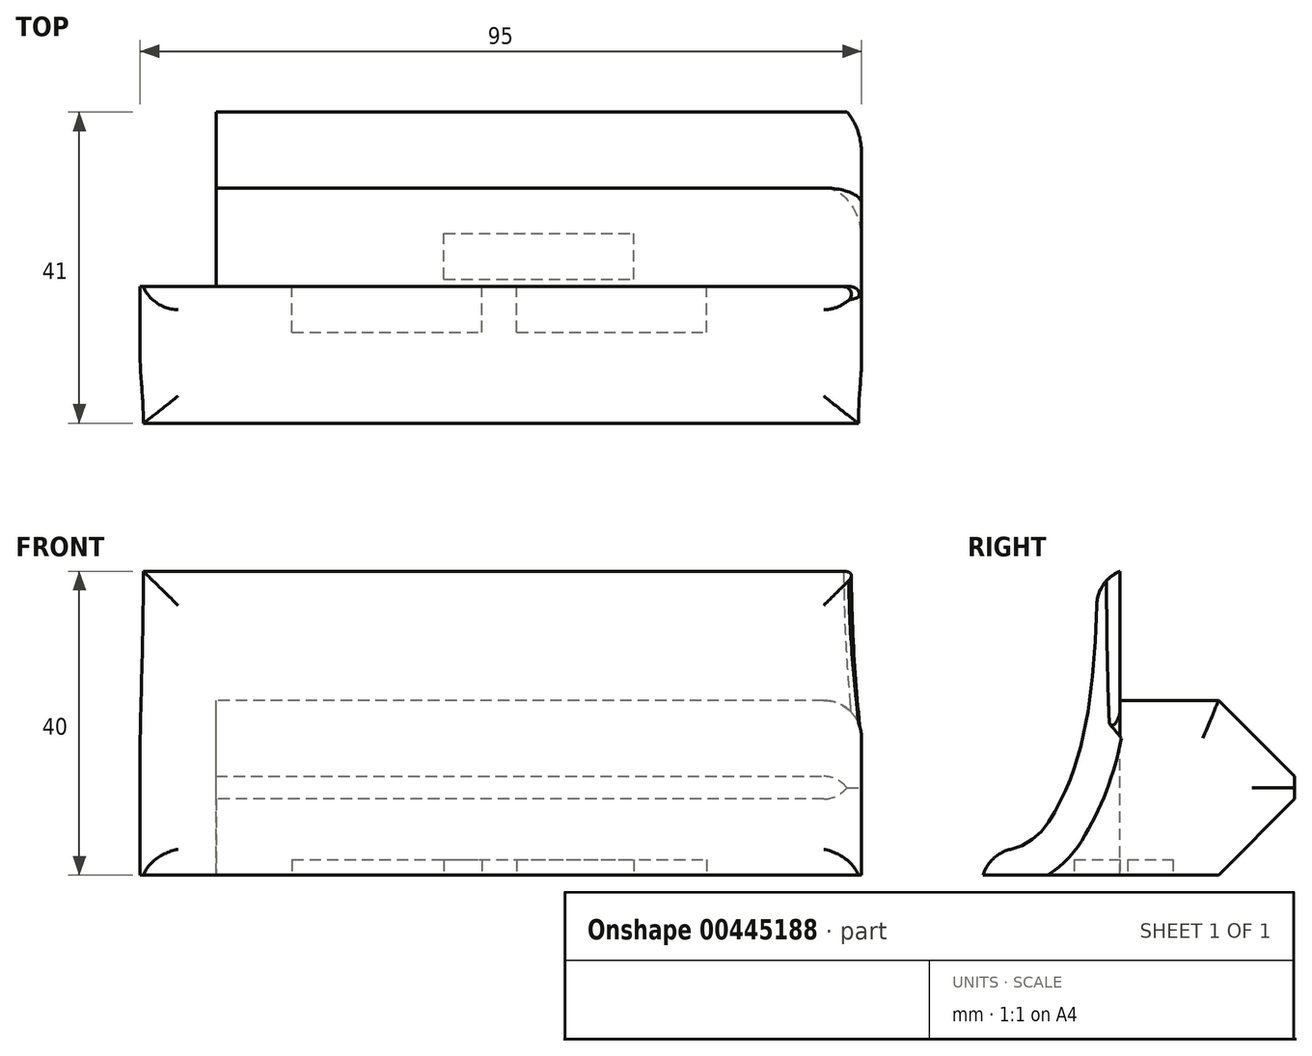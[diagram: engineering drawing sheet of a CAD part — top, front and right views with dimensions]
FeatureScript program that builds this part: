
annotation { "Feature Type Name" : "Feature", "Feature Type Description" : "" }
export const myFeature = defineFeature(function(context is Context, id is Id, definition is map)
    precondition{}
    {
        {
            var Q0;
            Q0=qCreatedBy(makeId("Right.planeOp"),FACE);
            var sketch = newSketch(context, id + "F0", { "sketchPlane" : qUnion([Q0])});
            skLineSegment(sketch, "E0", {"start": v(0, 0) * mm, "end": v(-18, 0) * mm});
            skLineSegment(sketch, "E1", {"start": v(0, 0) * mm, "end": v(0, 40) * mm});
            skLineSegment(sketch, "E2", {"start": v(0, 0) * mm, "end": v(-8.49, 8.49) * mm, "construction": true});
            skLineSegment(sketch, "E3", {"start": v(-18, 0) * mm, "end": v(-18, 3) * mm});
            skLineSegment(sketch, "E4", {"start": v(0, 40) * mm, "end": v(-3, 40) * mm});
            skFitSpline(sketch, "E5", {"points": [v(-18, 3) * mm, v(-8.49, 8.49) * mm, v(-3, 40) * mm], "startDerivative": vector(48.72, 0) * mm, "endDerivative": vector(0, 90.4) * mm});
            skLineSegment(sketch, "E6", {"start": v(0, 0) * mm, "end": v(23, 0) * mm});
            skLineSegment(sketch, "E7", {"start": v(23, 0) * mm, "end": v(23, 23) * mm});
            skLineSegment(sketch, "E8", {"start": v(23, 23) * mm, "end": v(0, 23) * mm});
            skSolve(sketch);
        }
        {
            var Q0;
            Q0 = qSketchRegion(id + "F0", true);
            extrude(context, id + "F1", {"entities" : qUnion([Q0]), "depth" : 85 * mm});
        }
        {
            var Q0;
            {var subQ3=sQuery(id+"F0.wireOp",EDGE,"E0");Q0=makeQuery(id+"F0.imprint","IMPRINT",FACE,{"disambiguationData":[TD([[makeQuery(id+"F0.imprint","IMPRINT",EDGE,{"derivedFrom":subQ3}),-1.0]])]});}
            extrude(context, id + "F2", {"entities" : qUnion([Q0]), "operationType" : NewBodyOperationType.ADD, "oppositeDirection" : true, "depth" : 10 * mm});
        }
        {
            var Q0;
            Q0=makeQuery(id+"F1.opExtrude","SWEPT_EDGE",EDGE,{"disambiguationData":[OSD([sQuery(id+"F0.wireOp",EDGE,"E7"),sQuery(id+"F0.wireOp",EDGE,"E8")])]});
            var Q1;
            Q1=makeQuery(id+"F1.opExtrude","SWEPT_EDGE",EDGE,{"disambiguationData":[OSD([sQuery(id+"F0.wireOp",EDGE,"E6"),sQuery(id+"F0.wireOp",EDGE,"E7")])]});
            chamfer(context, id + "F3", {"entities" : qUnion([Q0, Q1]), "width" : 10 * mm, "tangentPropagation" : true});
        }
        {
            var Q0;
            {var subQ0=sQuery(id+"F0.wireOp",EDGE,"E5");var subQ1=sQuery(id+"F0.wireOp",EDGE,"E3");Q0=makeQuery(id+"F2.boolean.opBoolean","MERGE",EDGE,{"derivedFrom":[makeQuery(id+"F1.opExtrude","SWEPT_EDGE",EDGE,{"disambiguationData":[OSD([subQ1,subQ0])]}),makeQuery(id+"F2.opExtrude","SWEPT_EDGE",EDGE,{"disambiguationData":[OSD([subQ1,subQ0])]})]});}
            var Q1;
            {var subQ0=sQuery(id+"F0.wireOp",EDGE,"E5");var subQ1=sQuery(id+"F0.wireOp",EDGE,"E4");Q1=makeQuery(id+"F2.boolean.opBoolean","MERGE",EDGE,{"derivedFrom":[makeQuery(id+"F1.opExtrude","SWEPT_EDGE",EDGE,{"disambiguationData":[OSD([subQ1,subQ0])]}),makeQuery(id+"F2.opExtrude","SWEPT_EDGE",EDGE,{"disambiguationData":[OSD([subQ1,subQ0])]})]});}
            var Q2;
            Q2=makeQuery(id+"F2.opExtrude","CAP_EDGE",EDGE,{"disambiguationData":[OSD([sQuery(id+"F0.wireOp",EDGE,"E5")])],"isStart":false});
            var Q3;
            Q3=makeQuery(id+"F1.opExtrude","CAP_EDGE",EDGE,{"disambiguationData":[OSD([sQuery(id+"F0.wireOp",EDGE,"E5")])],"isStart":false});
            var Q4;
            Q4=makeQuery(id+"F1.opExtrude","CAP_EDGE",EDGE,{"disambiguationData":[OSD([sQuery(id+"F0.wireOp",EDGE,"E8")])],"isStart":false});
            var Q5;
            Q5=makeQuery(id+"F1.opExtrude","CAP_EDGE",EDGE,{"disambiguationData":[OSD([sQuery(id+"F0.wireOp",EDGE,"E7")])],"isStart":false});
            var Q6;
            {var subQ0=sQuery(id+"F0.wireOp",EDGE,"E8");var subQ1=sQuery(id+"F0.wireOp",EDGE,"E7");Q6=makeQuery(id+"F3.opChamfer","BLEND_EDGE",EDGE,{"blendedFrom":[makeQuery(id+"F1.opExtrude","SWEPT_EDGE",EDGE,{"disambiguationData":[OSD([subQ1,subQ0])]}),makeQuery(id+"F1.opExtrude","CAP_FACE",FACE,{"disambiguationData":[OSD([sQuery(id+"F0.wireOp",EDGE,"E0"),sQuery(id+"F0.wireOp",EDGE,"E1"),sQuery(id+"F0.wireOp",EDGE,"E3"),sQuery(id+"F0.wireOp",EDGE,"E4"),sQuery(id+"F0.wireOp",EDGE,"E5"),sQuery(id+"F0.wireOp",EDGE,"E6"),subQ1,subQ0])],"isStart":false})],"blendedInto":[makeQuery(id+"F1.opExtrude","CAP_FACE",FACE,{"disambiguationData":[OSD([sQuery(id+"F0.wireOp",EDGE,"E0"),sQuery(id+"F0.wireOp",EDGE,"E1"),sQuery(id+"F0.wireOp",EDGE,"E3"),sQuery(id+"F0.wireOp",EDGE,"E4"),sQuery(id+"F0.wireOp",EDGE,"E5"),sQuery(id+"F0.wireOp",EDGE,"E6"),subQ1,subQ0])],"isStart":false})]});}
            var Q7;
            {var subQ0=sQuery(id+"F0.wireOp",EDGE,"E7");var subQ1=sQuery(id+"F0.wireOp",EDGE,"E6");Q7=makeQuery(id+"F3.opChamfer","BLEND_EDGE",EDGE,{"blendedFrom":[makeQuery(id+"F1.opExtrude","SWEPT_EDGE",EDGE,{"disambiguationData":[OSD([subQ1,subQ0])]}),makeQuery(id+"F1.opExtrude","CAP_FACE",FACE,{"disambiguationData":[OSD([sQuery(id+"F0.wireOp",EDGE,"E0"),sQuery(id+"F0.wireOp",EDGE,"E1"),sQuery(id+"F0.wireOp",EDGE,"E3"),sQuery(id+"F0.wireOp",EDGE,"E4"),sQuery(id+"F0.wireOp",EDGE,"E5"),subQ1,subQ0,sQuery(id+"F0.wireOp",EDGE,"E8")])],"isStart":false})],"blendedInto":[makeQuery(id+"F1.opExtrude","CAP_FACE",FACE,{"disambiguationData":[OSD([sQuery(id+"F0.wireOp",EDGE,"E0"),sQuery(id+"F0.wireOp",EDGE,"E1"),sQuery(id+"F0.wireOp",EDGE,"E3"),sQuery(id+"F0.wireOp",EDGE,"E4"),sQuery(id+"F0.wireOp",EDGE,"E5"),subQ1,subQ0,sQuery(id+"F0.wireOp",EDGE,"E8")])],"isStart":false})]});}
            fillet(context, id + "F4", {"entities" : qUnion([Q0, Q1, Q2, Q3, Q4, Q5, Q6, Q7]), "radius" : 5 * mm, "tangentPropagation" : true, "allowEdgeOverflow" : false});
        }
        {
            var Q0;
            {var subQ0=sQuery(id+"F0.wireOp",EDGE,"E1");Q0=makeQuery(id+"F4.opFillet","BLEND_EDGE",EDGE,{"blendedFrom":[makeQuery(id+"F1.opExtrude","CAP_EDGE",EDGE,{"disambiguationData":[OSD([sQuery(id+"F0.wireOp",EDGE,"E5")])],"isStart":false}),makeQuery(id+"F2.boolean.opBoolean","MERGE",FACE,{"derivedFrom":[makeQuery(id+"F1.opExtrude","SWEPT_FACE",FACE,{"disambiguationData":[OSD([subQ0])]}),makeQuery(id+"F2.opExtrude","SWEPT_FACE",FACE,{"disambiguationData":[OSD([subQ0])]})]})],"blendedInto":[makeQuery(id+"F2.boolean.opBoolean","MERGE",FACE,{"derivedFrom":[makeQuery(id+"F1.opExtrude","SWEPT_FACE",FACE,{"disambiguationData":[OSD([subQ0])]}),makeQuery(id+"F2.opExtrude","SWEPT_FACE",FACE,{"disambiguationData":[OSD([subQ0])]})]})]});}
            var Q1;
            {var subQ0=sQuery(id+"F0.wireOp",EDGE,"E8");var subQ1=sQuery(id+"F0.wireOp",EDGE,"E7");Q1=makeQuery(id+"F3.opChamfer","BLEND_EDGE",EDGE,{"blendedFrom":[makeQuery(id+"F1.opExtrude","SWEPT_EDGE",EDGE,{"disambiguationData":[OSD([subQ1,subQ0])]}),makeQuery(id+"F1.opExtrude","CAP_FACE",FACE,{"disambiguationData":[OSD([sQuery(id+"F0.wireOp",EDGE,"E0"),sQuery(id+"F0.wireOp",EDGE,"E1"),sQuery(id+"F0.wireOp",EDGE,"E3"),sQuery(id+"F0.wireOp",EDGE,"E4"),sQuery(id+"F0.wireOp",EDGE,"E5"),sQuery(id+"F0.wireOp",EDGE,"E6"),subQ1,subQ0])],"isStart":false})],"blendedInto":[makeQuery(id+"F1.opExtrude","CAP_FACE",FACE,{"disambiguationData":[OSD([sQuery(id+"F0.wireOp",EDGE,"E0"),sQuery(id+"F0.wireOp",EDGE,"E1"),sQuery(id+"F0.wireOp",EDGE,"E3"),sQuery(id+"F0.wireOp",EDGE,"E4"),sQuery(id+"F0.wireOp",EDGE,"E5"),sQuery(id+"F0.wireOp",EDGE,"E6"),subQ1,subQ0])],"isStart":false})]});}
            fillet(context, id + "F5", {"entities" : qUnion([Q0, Q1]), "radius" : 1 * mm, "tangentPropagation" : true, "allowEdgeOverflow" : false});
        }
        {
            var Q0;
            {var subQ0=sQuery(id+"F0.wireOp",EDGE,"E0");Q0=makeQuery(id+"F2.boolean.opBoolean","MERGE",FACE,{"derivedFrom":[makeQuery(id+"F1.opExtrude","SWEPT_FACE",FACE,{"disambiguationData":[OSD([subQ0,sQuery(id+"F0.wireOp",EDGE,"E6")])]}),makeQuery(id+"F2.opExtrude","SWEPT_FACE",FACE,{"disambiguationData":[OSD([subQ0])]})]});}
            var sketch = newSketch(context, id + "F6", { "sketchPlane" : qUnion([Q0])});
            skLineSegment(sketch, "E9.bottom", {"start": v(39.6, 6) * mm, "end": v(64.6, 6) * mm});
            skLineSegment(sketch, "E9.top", {"start": v(39.6, 0) * mm, "end": v(64.6, 0) * mm});
            skLineSegment(sketch, "E9.left", {"start": v(39.6, 6) * mm, "end": v(39.6, 0) * mm});
            skLineSegment(sketch, "E9.right", {"start": v(64.6, 6) * mm, "end": v(64.6, 0) * mm});
            skLineSegment(sketch, "E10.bottom", {"start": v(30, -1) * mm, "end": v(55, -1) * mm});
            skLineSegment(sketch, "E10.top", {"start": v(30, -7) * mm, "end": v(55, -7) * mm});
            skLineSegment(sketch, "E10.left", {"start": v(30, -1) * mm, "end": v(30, -7) * mm});
            skLineSegment(sketch, "E10.right", {"start": v(55, -1) * mm, "end": v(55, -7) * mm});
            skLineSegment(sketch, "E11.bottom", {"start": v(10, 6) * mm, "end": v(35, 6) * mm});
            skLineSegment(sketch, "E11.top", {"start": v(10, 0) * mm, "end": v(35, 0) * mm});
            skLineSegment(sketch, "E11.left", {"start": v(10, 6) * mm, "end": v(10, 0) * mm});
            skLineSegment(sketch, "E11.right", {"start": v(35, 6) * mm, "end": v(35, 0) * mm});
            skSolve(sketch);
        }
        {
            var Q0;
            Q0=makeQuery(id+"F6.imprint","IMPRINT",FACE,{"disambiguationData":[TD([[makeQuery(id+"F6.imprint","IMPRINT",EDGE,{"derivedFrom":sQuery(id+"F6.wireOp",EDGE,"E10.bottom")}),-1.0]])]});
            var Q1;
            Q1=makeQuery(id+"F6.imprint","IMPRINT",FACE,{"disambiguationData":[TD([[makeQuery(id+"F6.imprint","IMPRINT",EDGE,{"derivedFrom":sQuery(id+"F6.wireOp",EDGE,"E9.bottom")}),-1.0]])]});
            var Q2;
            Q2=makeQuery(id+"F6.imprint","IMPRINT",FACE,{"disambiguationData":[TD([[makeQuery(id+"F6.imprint","IMPRINT",EDGE,{"derivedFrom":sQuery(id+"F6.wireOp",EDGE,"E11.bottom")}),-1.0]])]});
            extrude(context, id + "F7", {"entities" : qUnion([Q0, Q1, Q2]), "operationType" : NewBodyOperationType.REMOVE, "oppositeDirection" : true, "depth" : 2 * mm});
        }
    });
